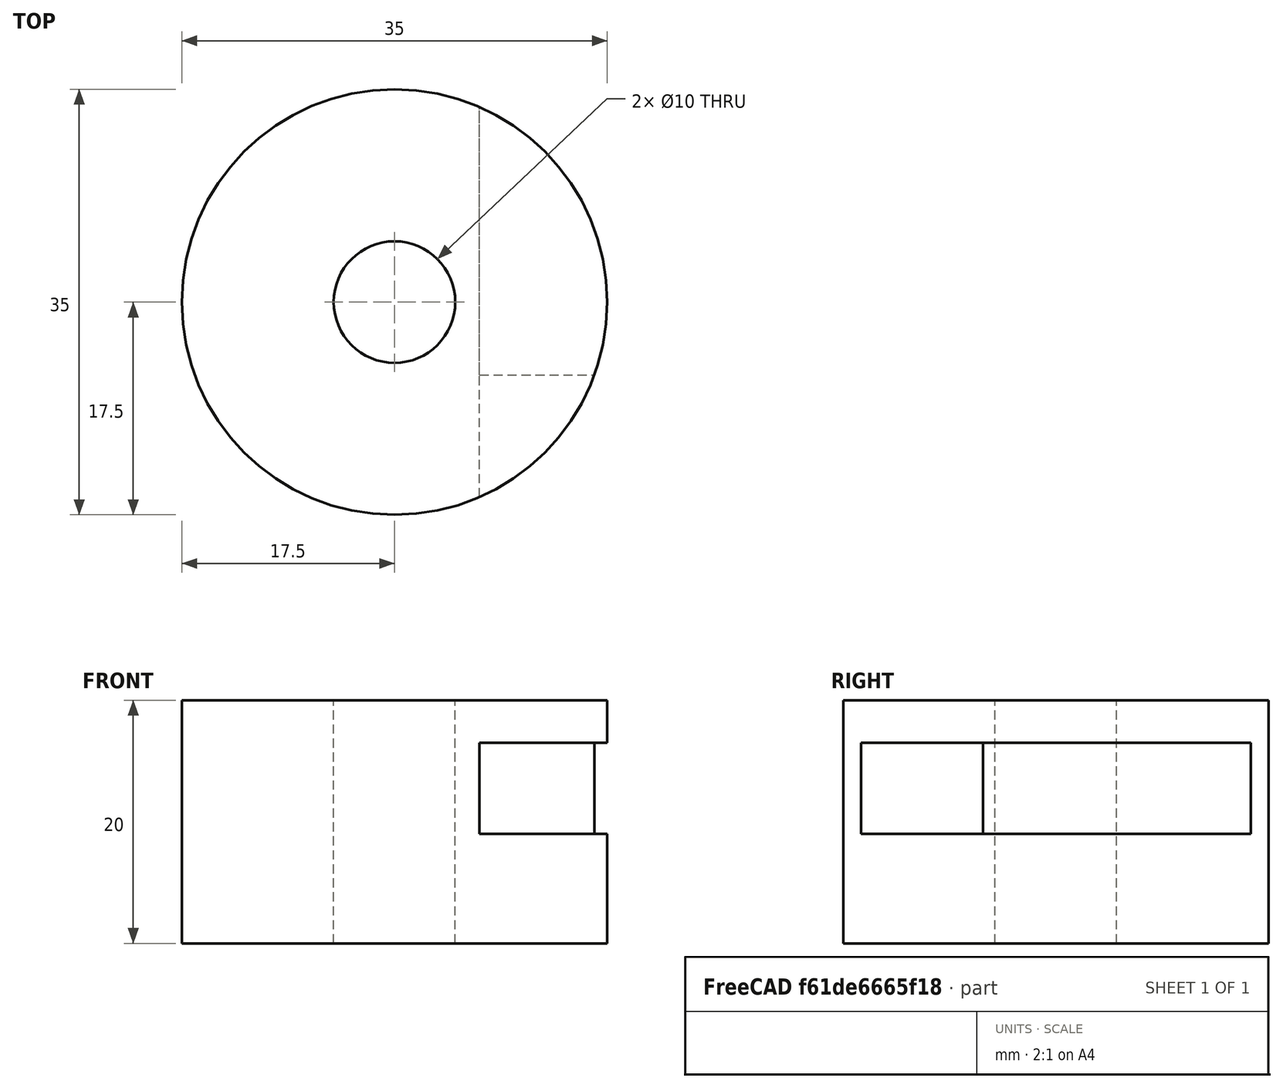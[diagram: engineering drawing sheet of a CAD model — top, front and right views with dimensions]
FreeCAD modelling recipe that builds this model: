
FCSTD DOCUMENT  (FreeCAD 0.15R4671 (Git))
Label: mounting-hardware
License: All rights reserved
LicenseURL: http://en.wikipedia.org/wiki/All_rights_reserved
objects: Drawing::FeatureView×8, Drawing::FeatureViewPart×7, Part::Cylinder×6, Part::Cut×6, Part::Box×3, Drawing::FeaturePage×1
note: 15 computed .brp shape members not serialized (recipe doc carries the construction recipe); baked Part::Feature solids carry a one-line shape summary decoded from their .brp

FEATURE [Part::Cylinder] Cylinder
  Angle = 360
  Height = 20
  Radius = 17.5
FEATURE [Part::Cylinder] Cylinder001
  Angle = 360
  Height = 40
  Placement = pos=(0,0,-10) rot=(0,0,1;0rad)
  Radius = 5
FEATURE [Part::Cut] Cut
  Base = -> Cylinder
  Tool = -> Cylinder001
FEATURE [Part::Box] Box  label="Cube"
  Height = 7.5
  Length = 30
  Placement = pos=(7,-6,9) rot=(0,0,1;0rad)
  Width = 30
FEATURE [Part::Cut] Cut001  label="Mount (Bottom R)"
  Base = -> Cut
  Tool = -> Box
FEATURE [Part::Cylinder] Cylinder002
  Angle = 360
  Height = 20
  Radius = 17.5
FEATURE [Part::Cylinder] Cylinder003
  Angle = 360
  Height = 40
  Placement = pos=(0,0,-10) rot=(0,0,1;0rad)
  Radius = 5
FEATURE [Part::Cut] Cut002
  Base = -> Cylinder002
  Tool = -> Cylinder003
FEATURE [Part::Box] Box001  label="Cube001"
  Height = 7.5
  Length = 30
  Placement = pos=(7,-20,9) rot=(0,0,1;0rad)
  Width = 70
FEATURE [Part::Cut] Cut003  label="Mount (Top L/R)"
  Base = -> Cut002
  Tool = -> Box001
FEATURE [Drawing::FeatureViewPart] View  label="Bottom - Front"
  Direction = (0,0,1)
  HiddenWidth = 0.15
  LineWidth = 0.35
  Rotation = 0
  ShowHiddenLines = true
  ShowSmoothLines = false
  Source = -> Cut001
  Tolerance = 0.05
  ViewResult = <g id="Bottom - Front"\n   transform="rotate(0,70,50) translate(70,50) scale(1,1)"\n  >\n<g   stroke="rgb(0, 0, 0)"\n   stroke-width="0.15"\n   stroke-linecap="butt"\n   stroke-linejoin="miter"\n   stroke-dasharray="0.2,0.1"\n   fill="none"\n   transform="scale(1,-1)"\n  >\n<path d="M16.4393 -6 A17.5 17.5 0 0 1 17.5 -4.28626e-015" /><path d="M16.4393 -6 A17.5 17.5 0 0 1 17.5 -4.28626e-015" /><circle cx ="0" cy ="0" r ="17.5" /><path d="M17.5 0 A17.5 17.5 0 0 1 7 16.039" /><path d="M17.5 0 A17.5 17.5 0 0 1 7 16.039" /><path id= "6" d=" M 7 -6 L 7 16.039 " />\n<path id= "7" d=" M 7 -6 L 16.4393 -6 " />\n<path id= "8" d=" M 7 -6 L 16.4393 -6 " />\n<path id= "9" d=" M 7 -6 L 7 16.039 " />\n<circle cx ="0" cy ="0" r ="5" /></g>\n<g   stroke="rgb(0, 0, 0)"\n   stroke-width="0.35"\n   stroke-linecap="butt"\n   stroke-linejoin="miter"\n   fill="none"\n   transform="scale(1,-1)"\n  >\n<circle cx ="0" cy ="0" r ="17.5" /><circle cx ="0" cy ="0" r ="5" /></g>\n</g>
  Visible = true
  X = 70
  Y = 50
FEATURE [Drawing::FeatureViewPart] View001  label="Top - Front"
  Direction = (0,0,1)
  HiddenWidth = 0.15
  LineWidth = 0.35
  Rotation = 0
  ShowHiddenLines = true
  ShowSmoothLines = false
  Source = -> Cut003
  Tolerance = 0.05
  ViewResult = <g id="Top - Front"\n   transform="rotate(0,70,120) translate(70,120) scale(1,1)"\n  >\n<g   stroke="rgb(0, 0, 0)"\n   stroke-width="0.15"\n   stroke-linecap="butt"\n   stroke-linejoin="miter"\n   stroke-dasharray="0.2,0.1"\n   fill="none"\n   transform="scale(1,-1)"\n  >\n<path d="M7 -16.039 A17.5 17.5 0 0 1 17.5 -4.28626e-015" /><path d="M7 -16.039 A17.5 17.5 0 0 1 17.5 -4.28626e-015" /><circle cx ="0" cy ="0" r ="17.5" /><path d="M17.5 0 A17.5 17.5 0 0 1 7 16.039" /><path d="M17.5 0 A17.5 17.5 0 0 1 7 16.039" /><path id= "6" d=" M 7 -16.039 L 7 16.039 " />\n<path id= "7" d=" M 7 -16.039 L 7 16.039 " />\n<circle cx ="0" cy ="0" r ="5" /></g>\n<g   stroke="rgb(0, 0, 0)"\n   stroke-width="0.35"\n   stroke-linecap="butt"\n   stroke-linejoin="miter"\n   fill="none"\n   transform="scale(1,-1)"\n  >\n<circle cx ="0" cy ="0" r ="17.5" /><circle cx ="0" cy ="0" r ="5" /></g>\n</g>
  Visible = true
  X = 70
  Y = 120
FEATURE [Drawing::FeatureViewPart] View002  label="Top - Side"
  Direction = (1,0,0)
  HiddenWidth = 0.15
  LineWidth = 0.35
  Rotation = 180
  ShowHiddenLines = true
  ShowSmoothLines = false
  Source = -> Cut003
  Tolerance = 0.05
  ViewResult = <blob: 4388 chars omitted>
  Visible = true
  X = 160
  Y = 120
FEATURE [Drawing::FeatureViewPart] View003  label="Bottom - Side"
  Direction = (1,0,0)
  HiddenWidth = 0.15
  LineWidth = 0.35
  Rotation = 180
  ShowHiddenLines = false
  ShowSmoothLines = false
  Source = -> Cut001
  Tolerance = 0.05
  ViewResult = <blob: 2232 chars omitted>
  Visible = true
  X = 160
  Y = 50
FEATURE [Drawing::FeatureViewPart] View004  label="Bottom - Ortho"
  Direction = (1,1,1)
  HiddenWidth = 0.15
  LineWidth = 0.35
  Rotation = 0
  ShowHiddenLines = false
  ShowSmoothLines = false
  Source = -> Cut001
  Tolerance = 0.05
  ViewResult = <g id="Bottom - Ortho"\n   transform="rotate(0,215,60) translate(215,60) scale(1,1)"\n  >\n<g   stroke="rgb(0, 0, 0)"\n   stroke-width="0.35"\n   stroke-linecap="butt"\n   stroke-linejoin="miter"\n   fill="none"\n   transform="scale(1,-1)"\n  >\n<path id= "1" d=" M -8.75 15.1554 L -22.8921 6.99048 " />\n<path id= "2" d=" M 8.75 -15.1554 L -5.39214 -23.3204 " />\n</g>\n<g   stroke="rgb(0, 0, 0)"\n   stroke-width="0.35"\n   stroke-linecap="butt"\n   stroke-linejoin="miter"\n   fill="none"\n   transform="scale(1,-1)"\n  >\n<path d="M-0.042934 -18.3464 A17.5 10.1036 120 0 1 0.707107 -13.8804" />\n<path id= "2" d=" M 5.26037 -15.2845 L -0.042934 -18.3464 " />\n<path d="M5.26037 -15.2845 A17.5 10.1036 120 0 1 6.01041 -10.8186" />\n<path d="M12.3744 -7.14435 A17.5 10.1036 120 0 1 -8.75 15.1554" />\n<path d="M8.75 -15.1554 A17.5 10.1036 120 0 1 12.3744 -7.14435" />\n<path d="M6.01041 -10.8186 A17.5 10.1036 120 0 1 -1.41421 6.56383" />\n<path id= "7" d=" M -1.41421 6.56383 L -6.71751 3.50197 " />\n<path d="M0.707107 -13.8804 A17.5 10.1036 120 0 1 -6.71751 3.50197" />\n<path d="M-1.76777 -15.3093 A17.5 10.1036 120 0 1 -22.8921 6.99048" />\n<path d="M-22.8921 6.99048 A17.5 10.1036 120 0 1 -5.39214 -23.3204" />\n<path d="M-5.39214 -23.3204 A17.5 10.1036 120 0 1 -1.76777 -15.3093" />\n<path id= "12" d=" M 0.661566 -12.6294 L 5.26037 -15.2845 " />\n<path id= "13" d=" M -1.41421 -4.6557 L -1.41421 6.56383 " />\n<path d="M-10.6066 -10.2062 A5 2.88675 120 0 1 -16.6421 -3.83484" />\n<path d="M-16.6421 -3.83484 A5 2.88675 120 0 1 -11.6421 -12.4951" />\n<path d="M-11.6421 -12.4951 A5 2.88675 120 0 1 -10.6066 -10.2062" />\n</g>\n</g>
  Visible = true
  X = 215
  Y = 60
FEATURE [Drawing::FeatureViewPart] View005  label="Top - Ortho"
  Direction = (1,1,1)
  HiddenWidth = 0.15
  LineWidth = 0.35
  Rotation = 0
  ShowHiddenLines = false
  ShowSmoothLines = false
  Source = -> Cut003
  Tolerance = 0.05
  ViewResult = <g id="Top - Ortho"\n   transform="rotate(0,240,115) translate(240,115) scale(1,1)"\n  >\n<g   stroke="rgb(0, 0, 0)"\n   stroke-width="0.35"\n   stroke-linecap="butt"\n   stroke-linejoin="miter"\n   fill="none"\n   transform="scale(1,-1)"\n  >\n<path id= "1" d=" M -8.75 15.1554 L -22.8921 6.99048 " />\n<path id= "2" d=" M 8.75 -15.1554 L 2.38604 -18.8297 " />\n<path id= "3" d=" M -2.91726 -21.8915 L -5.39214 -23.3204 " />\n</g>\n<g   stroke="rgb(0, 0, 0)"\n   stroke-width="0.35"\n   stroke-linecap="butt"\n   stroke-linejoin="miter"\n   fill="none"\n   transform="scale(1,-1)"\n  >\n<path d="M-2.91726 -21.8915 A17.5 10.1036 120 0 1 0.707107 -13.8804" />\n<path d="M-0.677071 -19.6479 A17.5 10.1036 120 0 1 2.38604 -18.8297" />\n<path d="M2.38604 -18.8297 A17.5 10.1036 120 0 1 6.01041 -10.8186" />\n<path d="M12.3744 -7.14435 A17.5 10.1036 120 0 1 -8.75 15.1554" />\n<path d="M8.75 -15.1554 A17.5 10.1036 120 0 1 12.3744 -7.14435" />\n<path d="M6.01041 -10.8186 A17.5 10.1036 120 0 1 -1.41421 6.56383" />\n<path id= "7" d=" M -1.41421 6.56383 L -6.71751 3.50197 " />\n<path d="M0.707107 -13.8804 A17.5 10.1036 120 0 1 -6.71751 3.50197" />\n<path d="M-1.76777 -15.3093 A17.5 10.1036 120 0 1 -22.8921 6.99048" />\n<path d="M-22.8921 6.99048 A17.5 10.1036 120 0 1 -5.39214 -23.3204" />\n<path d="M-5.39214 -23.3204 A17.5 10.1036 120 0 1 -1.76777 -15.3093" />\n<path id= "12" d=" M -1.41421 -4.6557 L -1.41421 6.56383 " />\n<path d="M-10.6066 -10.2062 A5 2.88675 120 0 1 -16.6421 -3.83484" />\n<path d="M-16.6421 -3.83484 A5 2.88675 120 0 1 -11.6421 -12.4951" />\n<path d="M-11.6421 -12.4951 A5 2.88675 120 0 1 -10.6066 -10.2062" />\n</g>\n</g>
  Visible = true
  X = 240
  Y = 115
FEATURE [Drawing::FeatureView] dim
  Rotation = 0
  ViewResult = <g>  <circle cx ="70.000000" cy ="50.000000" r="0.500000" stroke="none" fill="rgb(0,0,0)" /> \n<line x1="42.768659" y1="28.041715" x2="70.000000" y2="50.000000" style="stroke:rgb(0,0,0);stroke-width:0.30" />\n<polygon points="56.377167,39.015082 58.084800,41.676658 59.490957,41.525920 59.340219,40.119763" style="fill:rgb(0,0,0);stroke:rgb(0,0,0);stroke-width:0" />\n<line x1="42.768659" y1="28.041715" x2="32.076494" y2="28.041715" style="stroke:rgb(0,0,0);stroke-width:0.30" />\n<text x="37.422577" y="26.041715" font-family="arial" font-size="3.6" fill="rgb(0,0,0)" text-anchor="middle" transform="rotate(0.000000 37.422577,26.041715)" >R17.5</text> </g>
  Visible = true
  X = 0
  Y = 0
FEATURE [Drawing::FeatureView] dim001
  Rotation = 0
  ViewResult = <g> \n  <line x1="72.000000" y1="32.500000" x2="104.804067" y2="32.500000" style="stroke:rgb(0,0,0);stroke-width:0.30" />\n<line x1="88.439300" y1="56.000000" x2="104.804067" y2="56.000000" style="stroke:rgb(0,0,0);stroke-width:0.30" />\n<line x1="103.804067" y1="32.500000" x2="103.804067" y2="56.000000" style="stroke:rgb(0,0,0);stroke-width:0.30" /> \n  <polygon points="103.804067,56.000000 104.804067,53.000000 103.804067,52.000000 102.804067,53.000000" style="fill:rgb(0,0,0);stroke:rgb(0,0,0);stroke-width:0" /><polygon points="103.804067,32.500000 102.804067,35.500000 103.804067,36.500000 104.804067,35.500000" style="fill:rgb(0,0,0);stroke:rgb(0,0,0);stroke-width:0" /> \n  <text x="101.804067" y="44.250000" font-family="arial" font-size="3.6" fill="rgb(0,0,0)" text-anchor="middle" transform="rotate(-90.000000 101.804067,44.250000)" >23.5</text> </g>
  Visible = true
  X = 0
  Y = 0
FEATURE [Drawing::FeatureView] dim002
  Rotation = 0
  ViewResult = <g> \n  <line x1="70.000000" y1="69.500000" x2="70.000000" y2="80.081671" style="stroke:rgb(0,0,0);stroke-width:0.30" />\n<line x1="77.000000" y1="58.000000" x2="77.000000" y2="80.081671" style="stroke:rgb(0,0,0);stroke-width:0.30" />\n<line x1="70.000000" y1="79.081671" x2="77.000000" y2="79.081671" style="stroke:rgb(0,0,0);stroke-width:0.30" /> \n  <polygon points="77.000000,79.081671 80.000000,80.081671 81.000000,79.081671 80.000000,78.081671" style="fill:rgb(0,0,0);stroke:rgb(0,0,0);stroke-width:0" /><polygon points="70.000000,79.081671 67.000000,78.081671 66.000000,79.081671 67.000000,80.081671" style="fill:rgb(0,0,0);stroke:rgb(0,0,0);stroke-width:0" /> \n  <text x="73.500000" y="77.081671" font-family="arial" font-size="3.6" fill="rgb(0,0,0)" text-anchor="middle" transform="rotate(0.000000 73.500000,77.081671)" >7</text> </g>
  Visible = true
  X = 0
  Y = 0
FEATURE [Drawing::FeatureView] centerLines
  Rotation = 0
  ViewResult = <g transform="scale(1.000000,1.000000)" stroke="rgb(0,0,0)"  stroke-width="0.300000" > <path d="M 70.000000,50.000000 L 70.000000,52.000000 M 70.000000,54.000000 L 70.000000,60.000000 "/>\n<path d="M 70.000000,50.000000 L 72.000000,50.000000 M 74.000000,50.000000 L 80.000000,50.000000 "/>\n<path d="M 70.000000,50.000000 L 70.000000,48.000000 M 70.000000,46.000000 L 70.000000,40.000000 "/>\n<path d="M 70.000000,50.000000 L 68.000000,50.000000 M 66.000000,50.000000 L 60.000000,50.000000 "/> </g> 
  Visible = true
  X = 0
  Y = 0
FEATURE [Drawing::FeatureView] centerLines001
  Rotation = 0
  ViewResult = <g transform="scale(1.000000,1.000000)" stroke="rgb(0,0,0)"  stroke-width="0.300000" > <path d="M 70.000000,120.000000 L 70.000000,118.000000 M 70.000000,116.000000 L 70.000000,110.000000 "/>\n<path d="M 70.000000,120.000000 L 68.000000,120.000000 M 66.000000,120.000000 L 60.000000,120.000000 "/>\n<path d="M 70.000000,120.000000 L 70.000000,122.000000 M 70.000000,124.000000 L 70.000000,130.000000 "/>\n<path d="M 70.000000,120.000000 L 72.000000,120.000000 M 74.000000,120.000000 L 80.000000,120.000000 "/> </g> 
  Visible = true
  X = 0
  Y = 0
FEATURE [Drawing::FeatureView] dim003
  Rotation = 0
  ViewResult = <g> \n  <line x1="140.000000" y1="69.500000" x2="140.000000" y2="80.303158" style="stroke:rgb(0,0,0);stroke-width:0.30" />\n<line x1="160.000000" y1="69.500000" x2="160.000000" y2="80.303158" style="stroke:rgb(0,0,0);stroke-width:0.30" />\n<line x1="140.000000" y1="79.303158" x2="160.000000" y2="79.303158" style="stroke:rgb(0,0,0);stroke-width:0.30" /> \n  <polygon points="160.000000,79.303158 157.000000,78.303158 156.000000,79.303158 157.000000,80.303158" style="fill:rgb(0,0,0);stroke:rgb(0,0,0);stroke-width:0" /><polygon points="140.000000,79.303158 143.000000,80.303158 144.000000,79.303158 143.000000,78.303158" style="fill:rgb(0,0,0);stroke:rgb(0,0,0);stroke-width:0" /> \n  <text x="150.000000" y="77.303158" font-family="arial" font-size="3.6" fill="rgb(0,0,0)" text-anchor="middle" transform="rotate(0.000000 150.000000,77.303158)" >20</text> </g>
  Visible = true
  X = 0
  Y = 0
FEATURE [Drawing::FeatureView] dim004
  Rotation = 0
  ViewResult = <g> \n  <line x1="143.500000" y1="101.961000" x2="143.500000" y2="93.649391" style="stroke:rgb(0,0,0);stroke-width:0.30" />\n<line x1="151.000000" y1="101.961000" x2="151.000000" y2="93.649391" style="stroke:rgb(0,0,0);stroke-width:0.30" />\n<line x1="143.500000" y1="94.649391" x2="151.000000" y2="94.649391" style="stroke:rgb(0,0,0);stroke-width:0.30" /> \n  <polygon points="151.000000,94.649391 154.000000,95.649391 155.000000,94.649391 154.000000,93.649391" style="fill:rgb(0,0,0);stroke:rgb(0,0,0);stroke-width:0" /><polygon points="143.500000,94.649391 140.500000,93.649391 139.500000,94.649391 140.500000,95.649391" style="fill:rgb(0,0,0);stroke:rgb(0,0,0);stroke-width:0" /> \n  <text x="147.250000" y="92.649391" font-family="arial" font-size="3.6" fill="rgb(0,0,0)" text-anchor="middle" transform="rotate(0.000000 147.250000,92.649391)" >7.5</text> </g>
  Visible = true
  X = 0
  Y = 0
FEATURE [Drawing::FeatureView] dim005
  Rotation = 0
  ViewResult = <g> \n  <line x1="87.500000" y1="118.000000" x2="87.500000" y2="93.996707" style="stroke:rgb(0,0,0);stroke-width:0.30" />\n<line x1="77.000000" y1="101.961000" x2="77.000000" y2="93.996707" style="stroke:rgb(0,0,0);stroke-width:0.30" />\n<line x1="87.500000" y1="94.996707" x2="77.000000" y2="94.996707" style="stroke:rgb(0,0,0);stroke-width:0.30" /> \n  <polygon points="77.000000,94.996707 80.000000,95.996707 81.000000,94.996707 80.000000,93.996707" style="fill:rgb(0,0,0);stroke:rgb(0,0,0);stroke-width:0" /><polygon points="87.500000,94.996707 84.500000,93.996707 83.500000,94.996707 84.500000,95.996707" style="fill:rgb(0,0,0);stroke:rgb(0,0,0);stroke-width:0" /> \n  <text x="82.250000" y="92.996707" font-family="arial" font-size="3.6" fill="rgb(0,0,0)" text-anchor="middle" transform="rotate(0.000000 82.250000,92.996707)" >10.5</text> </g>
  Visible = true
  X = 0
  Y = 0
FEATURE [Part::Cylinder] Cylinder004
  Angle = 360
  Height = 20
  Radius = 17.5
FEATURE [Part::Cylinder] Cylinder005
  Angle = 360
  Height = 40
  Placement = pos=(0,0,-10) rot=(0,0,1;0rad)
  Radius = 5
FEATURE [Part::Cut] Cut004
  Base = -> Cylinder004
  Tool = -> Cylinder005
FEATURE [Part::Box] Box002  label="Cube002"
  Height = 7.5
  Length = 30
  Placement = pos=(-37,-6,9) rot=(0,0,1;0rad)
  Width = 30
FEATURE [Part::Cut] Cut005  label="Mount (Bottom L)"
  Base = -> Cut004
  Tool = -> Box002
FEATURE [Drawing::FeatureViewPart] View006  label="Bottom Left - Ortho"
  Direction = (-1,1,-1)
  HiddenWidth = 0.15
  LineWidth = 0.35
  Rotation = 0
  ShowHiddenLines = false
  ShowSmoothLines = false
  Source = -> Cut005
  Tolerance = 0.05
  ViewResult = <g id="Bottom Left - Ortho"\n   transform="rotate(0,240,50) translate(240,50) scale(1,1)"\n  >\n<g   stroke="rgb(0, 0, 0)"\n   stroke-width="0.35"\n   stroke-linecap="butt"\n   stroke-linejoin="miter"\n   fill="none"\n   transform="scale(1,-1)"\n  >\n<path id= "1" d=" M 8.75 -15.1554 L 22.8921 -6.99048 " />\n<path id= "2" d=" M -8.75 15.1554 L 5.39214 23.3204 " />\n</g>\n<g   stroke="rgb(0, 0, 0)"\n   stroke-width="0.35"\n   stroke-linecap="butt"\n   stroke-linejoin="miter"\n   fill="none"\n   transform="scale(1,-1)"\n  >\n<path d="M-12.3744 7.14435 A17.5 10.1036 -60 0 0 -8.75 15.1554" />\n<path d="M-8.75 15.1554 A17.5 10.1036 -60 0 0 8.75 -15.1554" />\n<path d="M8.75 -15.1554 A17.5 10.1036 -60 0 0 -12.3744 7.14435" />\n<path d="M5.39214 23.3204 A17.5 10.1036 -60 0 0 22.8921 -6.99048" />\n<path id= "5" d=" M 11.3137 13.9123 L 16.617 16.9742 " />\n<path d="M11.3137 13.9123 A17.5 10.1036 -60 0 0 17.9883 -7.93605" />\n<path id= "7" d=" M 17.9883 -7.93605 L 23.2916 -4.87419 " />\n<path d="M16.617 16.9742 A17.5 10.1036 -60 0 0 23.2916 -4.87419" />\n<path d="M-3.53553 2.04124 A5 2.88675 -60 0 0 -2.5 4.33013" />\n<path d="M-2.5 4.33013 A5 2.88675 -60 0 0 2.5 -4.33013" />\n<path d="M2.5 -4.33013 A5 2.88675 -60 0 0 -3.53553 2.04124" />\n<path id= "12" d=" M 16.617 5.75463 L 16.617 16.9742 " />\n<path id= "13" d=" M 23.2916 -4.87419 L 18.6928 -2.21907 " />\n</g>\n</g>
  Visible = true
  X = 240
  Y = 50
FEATURE [Drawing::FeaturePage] Page  label="Drawing"
  EditableTexts = FLOYD DIEBEL | 02/02/2016 | 1:1 | GROUNDED SIGN | Slotted Standoff Hardware | 01 | 02
  Group = -> [View,View003,View004,View005,View002,View001,dim,dim001,dim002,centerLines,centerLines001,dim003,dim004,dim005,View006]
  Template = D:/Program Files/FreeCAD 0.15/data/Mod/Drawing/Templates/A4_Landscape.svg
